# Revit family: Doorset_Entrance Door with Escape Control and Push Bar_ASSA ABLOY DE_Hardware Light
name_source: partatom
category: Doors
revit_build: Autodesk Revit 2015 (Build: 20140606_1530(x64)
units: mm (PartAtom-declared; Revit-internal decimal feet)

## types (7) — shared parameters
Architectural Hardware = 1x Knob (outside)_OneSystem_ASSA ABLOY
BIMobject Brand = ASSA ABLOY DE
BIMobject Instructions Video = https://www.youtube.com
BIMobject Product Family = Exterior Door Solutions
BIMobject Product Group = Single-Steel/Aluminium-Self Closing-Panic Device-Escape Route
BIMobject Product Page = http://bimobject.com
BIMobject Unique ref = ES1-ML-PE-ET-DC-DE10
Date of publishing = 22.09.2016
Description = Self Closing Door with Escape route technology
Door Closers = 1x Door Closer DC700 with guide rail_Cam-Motion®_ASSA ABLOY
Edition number = 1
Electronic Accessories = 1x Reed contact_10380A-6_Effeff
Frame Material = Steel/Aluminium
Function = Exterior
Hardware Set = ES1-ML-PE-ET-DC-DE10
IFC Classification = Door
Identity and Access Solutions = 1x Key Switch (outside) _Flush-mounted 1140_Effeff
Locksets = 1x Security Panic Lock_OneSystem_ASSA ABLOY
Manufacturer = ASSA ABLOY
Maximum Door Height = 3750 mm
Maximum Door Width = 1500 mm
Maximum Thickness = 105 mm
Minimum Door Height = 2110 mm
Minimum Door Width = 900 mm  [stored 2.95276 ft]
Minimum Thickness = 38 mm
Model = Doorset_Entrance Door w/ Escape Control and Push Bar_ASSA ABLOY DE_Hardware Light
NBS Reference Code = 59-23
NBS Reference Description = Doorsets
Name = Entrance Door w/ Escape Control and Push Bar
OmniClass Number = 23-17 11 00
OmniClass Title = Doors
Panel Material = Steel/Aluminium
Panic and Exit Devices_1 = 1x Push bar gear set (paddle)_OneSystem_ASSA ABLOY
Panic and Exit Devices_2 = 1x Door surveillance system_Flush-mounted 1385T_Effeff
Product Guid = 144a79a3-058c-4655-b260-41d7a545d461
Provider = ASSA ABLOY DE
Push Bar Distance From Handle = 125 mm
Push Bar Distance From Hinge = 125 mm
Thickness = 90 mm  [stored 0.295276 ft]
Thickness Constraint = 90 mm  [stored 0.295276 ft]
URL = http://www.assaabloy.de
Uniclass 1.4 Code = L411
Uniclass 1.4 Description = Doors
Uniclass 2.0 Code = PR-59-23
Uniclass 2.0 Description = Doorsets
Wall Closure = By host

## per-type parameters (varying)
| type | Frame Height | Frame Width | Height | Panel Height | Panel Width | Push Bar Length | Rough Height | Rough Width | Width |
| 900 x 2110 mm (1000 x 2160 mm) | 2160 mm | 1000 mm | 2160 mm | 2110 mm | 900 mm  [stored 2.95276 ft] | 650 mm  [stored 2.13255 ft] | 2172 mm | 1024 mm  [stored 3.35958 ft] | 1000 mm |
| 1000 x 2110 mm (1100 x 2160 mm) | 2160 mm | 1100 mm | 2160 mm | 2110 mm | 1000 mm | 750 mm | 2172 mm | 1124 mm | 1100 mm |
| 1000 x 2500 mm (1100 x 2550 mm) | 2550 mm | 1100 mm | 2550 mm | 2500 mm | 1000 mm | 750 mm | 2562 mm | 1124 mm | 1100 mm |
| 1000 x 3750 mm (1100 x 3800 mm) | 3800 mm | 1100 mm | 3800 mm | 3750 mm | 1000 mm | 750 mm | 3812 mm | 1124 mm | 1100 mm |
| 1300 x 2500 mm (1400 x 2550 mm) | 2550 mm | 1400 mm | 2550 mm | 2500 mm | 1300 mm | 1050 mm  [stored 3.44488 ft] | 2562 mm | 1424 mm | 1400 mm |
| 1300 x 3750 mm (1400 x 3800 mm) | 3800 mm | 1400 mm | 3800 mm | 3750 mm | 1300 mm | 1050 mm  [stored 3.44488 ft] | 3812 mm | 1424 mm | 1400 mm |
| 1500 x 3750 mm (1600 x 3800 mm) | 3800 mm | 1600 mm | 3800 mm | 3750 mm | 1500 mm | 1250 mm | 3812 mm | 1624 mm | 1600 mm |

note: column(s) folded — value = type name in every type: Type Comments

note: [stored X ft] marks values corroborated as IEEE doubles in the binary element streams (Revit-internal decimal feet)

## geometry (parser evidence)
native form markers: Blend x6, Sweep x2
no freeform markers — native parametric forms only
